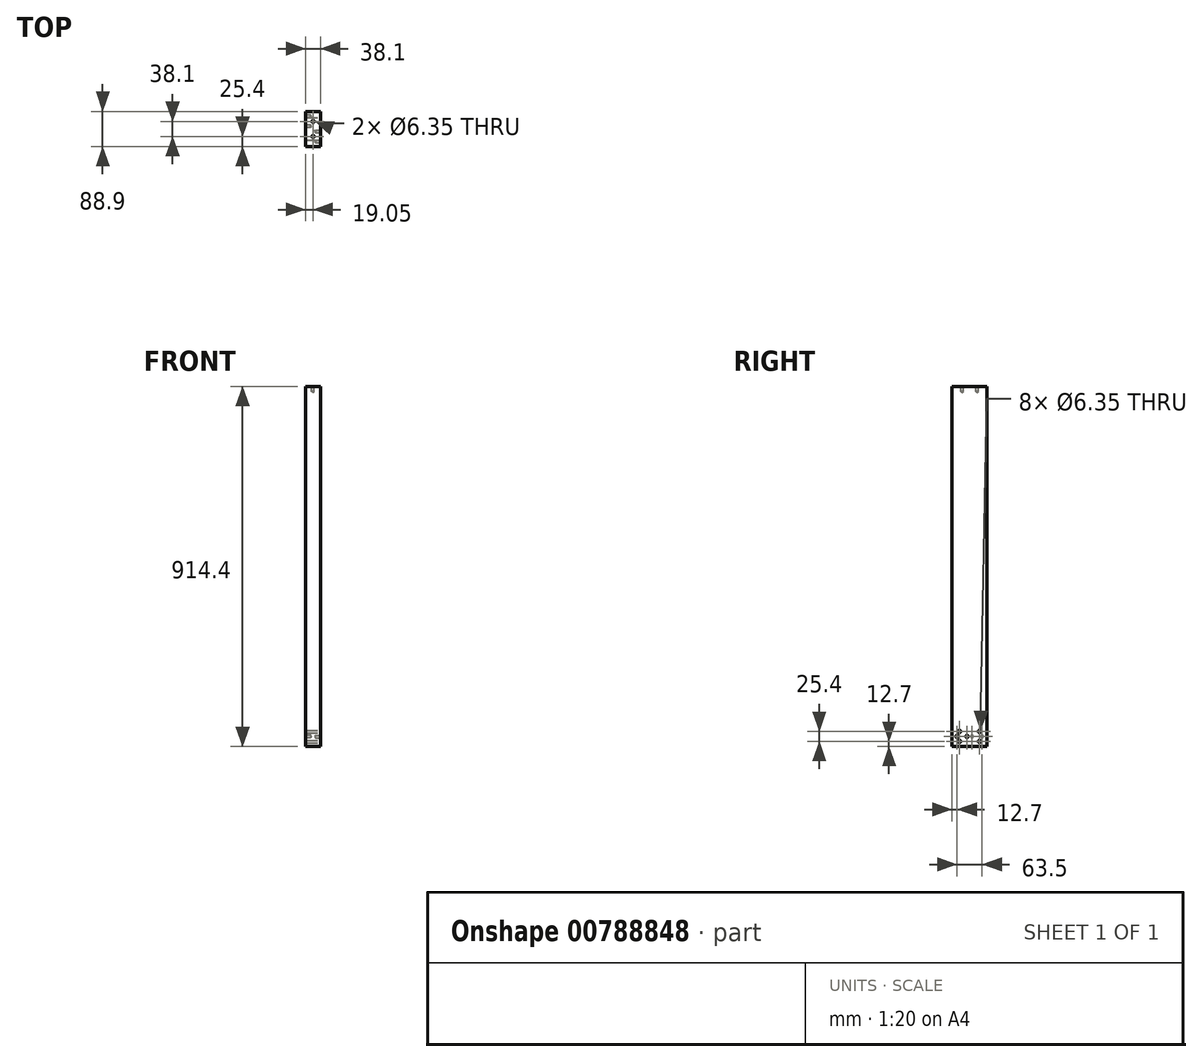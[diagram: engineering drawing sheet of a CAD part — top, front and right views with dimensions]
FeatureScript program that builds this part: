
annotation { "Feature Type Name" : "Feature", "Feature Type Description" : "" }
export const myFeature = defineFeature(function(context is Context, id is Id, definition is map)
    precondition{}
    {
        {
            var Q0;
            Q0=qCreatedBy(makeId("Right.planeOp"),FACE);
            var sketch = newSketch(context, id + "F0", { "sketchPlane" : qUnion([Q0])});
            skLineSegment(sketch, "E0.bottom", {"start": v(0, 0) * mm, "end": v(88.9, 0) * mm});
            skLineSegment(sketch, "E0.top", {"start": v(0, -914.4) * mm, "end": v(88.9, -914.4) * mm});
            skLineSegment(sketch, "E0.left", {"start": v(0, 0) * mm, "end": v(0, -914.4) * mm});
            skLineSegment(sketch, "E0.right", {"start": v(88.9, 0) * mm, "end": v(88.9, -914.4) * mm});
            skSolve(sketch);
        }
        {
            var Q0;
            Q0=makeQuery(id+"F0.imprint","IMPRINT",FACE,{"disambiguationData":[TD([[makeQuery(id+"F0.imprint","IMPRINT",EDGE,{"derivedFrom":sQuery(id+"F0.wireOp",EDGE,"E0.bottom")}),-1.0]])]});
            extrude(context, id + "F1", {"entities" : qUnion([Q0]), "depth" : 38.1 * mm, "offsetDistance" : 25.4 * mm});
        }
        {
            var Q0;
            Q0=makeQuery(id+"F1.opExtrude","CAP_FACE",FACE,{"disambiguationData":[OSD([sQuery(id+"F0.wireOp",EDGE,"E0.bottom"),sQuery(id+"F0.wireOp",EDGE,"E0.top"),sQuery(id+"F0.wireOp",EDGE,"E0.left"),sQuery(id+"F0.wireOp",EDGE,"E0.right")])],"isStart":false});
            var sketch = newSketch(context, id + "F2", { "sketchPlane" : qUnion([Q0])});
            skLineSegment(sketch, "E1", {"start": v(0, -876.3) * mm, "end": v(88.9, -876.3) * mm, "construction": true});
            skLineSegment(sketch, "E2", {"start": v(0, -901.7) * mm, "end": v(88.9, -901.7) * mm, "construction": true});
            skPoint(sketch, "E3", {"position": v(19.05, -876.3) * mm});
            skPoint(sketch, "E4", {"position": v(19.05, -901.7) * mm});
            skPoint(sketch, "E5", {"position": v(69.85, -876.3) * mm});
            skPoint(sketch, "E6", {"position": v(69.85, -901.7) * mm});
            skPoint(sketch, "E7", {"position": v(47, -876.3) * mm});
            skPoint(sketch, "E8", {"position": v(31.75, -901.7) * mm});
            skPoint(sketch, "E9", {"position": v(41.91, -876.3) * mm});
            skPoint(sketch, "E10", {"position": v(57.15, -901.7) * mm});
            skSolve(sketch);
        }
        {
            var Q0;
            Q0=sQuery(id+"F2.wireOp",VERTEX,"E3");
            var Q1;
            Q1=sQuery(id+"F2.wireOp",VERTEX,"E4");
            var Q2;
            Q2=sQuery(id+"F2.wireOp",VERTEX,"E5");
            var Q3;
            Q3=sQuery(id+"F2.wireOp",VERTEX,"E6");
            var Q4;
            Q4=makeQuery(id+"F1.opExtrude","SWEPT_BODY",BODY,{"disambiguationData":[OSD([sQuery(id+"F0.wireOp",EDGE,"E0.bottom"),sQuery(id+"F0.wireOp",EDGE,"E0.top"),sQuery(id+"F0.wireOp",EDGE,"E0.left"),sQuery(id+"F0.wireOp",EDGE,"E0.right")])]});
            hole(context, id + "F3", {"style" : HoleStyle.SIMPLE, "endStyle" : HoleEndStyle.THROUGH, "holeDiameter" : 6.35 * mm, "majorDiameter" : 6.35 * mm, "isTappedThrough" : true, "tappedDepth" : 12.7 * mm, "tapClearance" : 3, "locations" : qUnion([Q0, Q1, Q2, Q3]), "scope" : qUnion([Q4])});
        }
        {
            var Q0;
            Q0=makeQuery(id+"F1.opExtrude","CAP_FACE",FACE,{"disambiguationData":[OSD([sQuery(id+"F0.wireOp",EDGE,"E0.bottom"),sQuery(id+"F0.wireOp",EDGE,"E0.top"),sQuery(id+"F0.wireOp",EDGE,"E0.left"),sQuery(id+"F0.wireOp",EDGE,"E0.right")])],"isStart":true});
            var sketch = newSketch(context, id + "F4", { "sketchPlane" : qUnion([Q0])});
            skLineSegment(sketch, "E11", {"start": v(0, -889) * mm, "end": v(-88.9, -889) * mm, "construction": true});
            skLineSegment(sketch, "E12", {"start": v(-76.2, -914.4) * mm, "end": v(-76.2, -889) * mm, "construction": true});
            skLineSegment(sketch, "E13", {"start": v(-50.8, -914.4) * mm, "end": v(-50.8, -889) * mm, "construction": true});
            skSolve(sketch);
        }
        {
            var Q0;
            Q0=sQuery(id+"F4.wireOp",VERTEX,"E12.end");
            var Q1;
            Q1=sQuery(id+"F4.wireOp",VERTEX,"E13.end");
            var Q2;
            Q2=makeQuery(id+"F1.opExtrude","SWEPT_BODY",BODY,{"disambiguationData":[OSD([sQuery(id+"F0.wireOp",EDGE,"E0.bottom"),sQuery(id+"F0.wireOp",EDGE,"E0.top"),sQuery(id+"F0.wireOp",EDGE,"E0.left"),sQuery(id+"F0.wireOp",EDGE,"E0.right")])]});
            hole(context, id + "F5", {"style" : HoleStyle.SIMPLE, "endStyle" : HoleEndStyle.BLIND, "holeDiameter" : 6.35 * mm, "majorDiameter" : 6.35 * mm, "holeDepth" : 12.7 * mm, "isTappedThrough" : true, "tappedDepth" : 12.7 * mm, "tapClearance" : 3, "locations" : qUnion([Q0, Q1]), "scope" : qUnion([Q2])});
        }
        {
            var Q0;
            Q0=makeQuery(id+"F1.opExtrude","CAP_FACE",FACE,{"disambiguationData":[OSD([sQuery(id+"F0.wireOp",EDGE,"E0.bottom"),sQuery(id+"F0.wireOp",EDGE,"E0.top"),sQuery(id+"F0.wireOp",EDGE,"E0.left"),sQuery(id+"F0.wireOp",EDGE,"E0.right")])],"isStart":false});
            var sketch = newSketch(context, id + "F6", { "sketchPlane" : qUnion([Q0])});
            skLineSegment(sketch, "E14", {"start": v(0, -889) * mm, "end": v(88.9, -889) * mm, "construction": true});
            skPoint(sketch, "E15", {"position": v(38.1, -889) * mm});
            skPoint(sketch, "E16", {"position": v(12.7, -889) * mm});
            skLineSegment(sketch, "E17", {"start": v(44.45, -914.4) * mm, "end": v(44.45, -846.91) * mm, "construction": true});
            skSolve(sketch);
        }
        {
            var Q0;
            Q0=sQuery(id+"F6.wireOp",VERTEX,"E16");
            var Q1;
            Q1=sQuery(id+"F6.wireOp",VERTEX,"E15");
            var Q2;
            Q2=makeQuery(id+"F1.opExtrude","SWEPT_BODY",BODY,{"disambiguationData":[OSD([sQuery(id+"F0.wireOp",EDGE,"E0.bottom"),sQuery(id+"F0.wireOp",EDGE,"E0.top"),sQuery(id+"F0.wireOp",EDGE,"E0.left"),sQuery(id+"F0.wireOp",EDGE,"E0.right")])]});
            hole(context, id + "F7", {"style" : HoleStyle.SIMPLE, "endStyle" : HoleEndStyle.BLIND, "holeDiameter" : 6.35 * mm, "majorDiameter" : 6.35 * mm, "holeDepth" : 12.7 * mm, "isTappedThrough" : true, "tappedDepth" : 12.7 * mm, "tapClearance" : 3, "locations" : qUnion([Q0, Q1]), "scope" : qUnion([Q2])});
        }
        {
            var Q0;
            Q0=makeQuery(id+"F1.opExtrude","SWEPT_FACE",FACE,{"disambiguationData":[OSD([sQuery(id+"F0.wireOp",EDGE,"E0.bottom")])]});
            var sketch = newSketch(context, id + "F8", { "sketchPlane" : qUnion([Q0])});
            skLineSegment(sketch, "E18", {"start": v(19.05, 88.9) * mm, "end": v(19.05, 0) * mm, "construction": true});
            skPoint(sketch, "E19", {"position": v(19.05, 63.5) * mm});
            skPoint(sketch, "E20", {"position": v(19.05, 25.4) * mm});
            skSolve(sketch);
        }
        {
            var Q0;
            Q0=sQuery(id+"F8.wireOp",VERTEX,"E19");
            var Q1;
            Q1=sQuery(id+"F8.wireOp",VERTEX,"E20");
            var Q2;
            Q2=makeQuery(id+"F1.opExtrude","SWEPT_BODY",BODY,{"disambiguationData":[OSD([sQuery(id+"F0.wireOp",EDGE,"E0.bottom"),sQuery(id+"F0.wireOp",EDGE,"E0.top"),sQuery(id+"F0.wireOp",EDGE,"E0.left"),sQuery(id+"F0.wireOp",EDGE,"E0.right")])]});
            hole(context, id + "F9", {"style" : HoleStyle.SIMPLE, "endStyle" : HoleEndStyle.BLIND, "holeDiameter" : 6.35 * mm, "majorDiameter" : 6.35 * mm, "holeDepth" : 12.7 * mm, "isTappedThrough" : true, "tappedDepth" : 12.7 * mm, "tapClearance" : 3, "locations" : qUnion([Q0, Q1]), "scope" : qUnion([Q2])});
        }
    });
